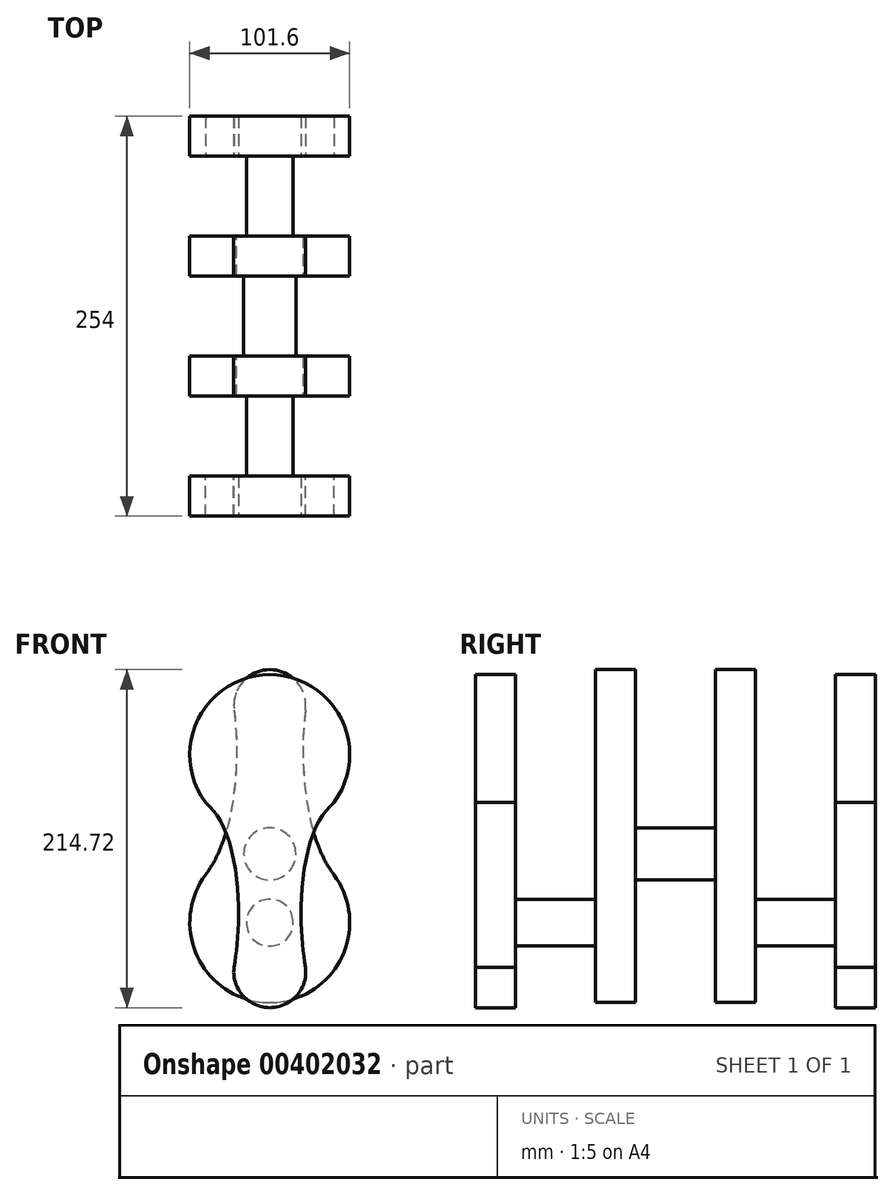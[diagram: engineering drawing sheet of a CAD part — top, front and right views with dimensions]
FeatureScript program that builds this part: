
annotation { "Feature Type Name" : "Feature", "Feature Type Description" : "" }
export const myFeature = defineFeature(function(context is Context, id is Id, definition is map)
    precondition{}
    {
        {
            var Q0;
            Q0=qCreatedBy(makeId("Front.planeOp"),FACE);
            var sketch = newSketch(context, id + "F0", { "sketchPlane" : qUnion([Q0])});
            skArc(sketch, "E0", {"start": v(-40.78, 30.29) * mm, "mid": v(0, -50.8) * mm, "end": v(40.78, 30.29) * mm});
            skArc(sketch, "E1", {"start": v(22.7, 135.07) * mm, "mid": v(0, 160.7) * mm, "end": v(-22.7, 135.07) * mm});
            skFitSpline(sketch, "E2", {"points": [v(-22.7, 135.07) * mm, v(-22.7, 83.37) * mm, v(-40.78, 30.29) * mm], "startDerivative": vector(13.12, -107.4) * mm, "endDerivative": vector(-66.36, -89.36) * mm});
            skLineSegment(sketch, "E3", {"start": v(0, 34.49) * mm, "end": v(0, 95.13) * mm, "construction": true});
            skFitSpline(sketch, "E4.MirrorCS", {"points": [v(22.7, 135.07) * mm, v(22.7, 83.37) * mm, v(40.78, 30.29) * mm], "startDerivative": vector(-13.12, -107.4) * mm, "endDerivative": vector(66.36, -89.36) * mm});
            skSolve(sketch);
        }
        {
            var Q0;
            Q0=makeQuery(id+"F0.imprint","IMPRINT",FACE,{"disambiguationData":[TD([[makeQuery(id+"F0.imprint","IMPRINT",EDGE,{"derivedFrom":sQuery(id+"F0.wireOp",EDGE,"E0")}),1.0]])]});
            extrude(context, id + "F1", {"entities" : qUnion([Q0]), "depth" : 25.4 * mm});
        }
        {
            var Q0;
            Q0=makeQuery(id+"F1.opExtrude","CAP_FACE",FACE,{"disambiguationData":[OSD([sQuery(id+"F0.wireOp",EDGE,"E0"),sQuery(id+"F0.wireOp",EDGE,"E1"),sQuery(id+"F0.wireOp",EDGE,"E2"),sQuery(id+"F0.wireOp",EDGE,"E4.MirrorCS")])],"isStart":false});
            var sketch = newSketch(context, id + "F2", { "sketchPlane" : qUnion([Q0])});
            skCircle(sketch, "E5", {"center": v(0, 0) * mm, "radius": 14.86 * mm});
            skSolve(sketch);
        }
        {
            var Q0;
            Q0 = qSketchRegion(id + "F2", true);
            extrude(context, id + "F3", {"entities" : qUnion([Q0]), "operationType" : NewBodyOperationType.ADD, "depth" : 50.8 * mm});
        }
        {
            var Q0;
            Q0=makeQuery(id+"F3.opExtrude","CAP_FACE",FACE,{"disambiguationData":[OSD([sQuery(id+"F2.wireOp",EDGE,"E5")])],"isStart":false});
            var sketch = newSketch(context, id + "F4", { "sketchPlane" : qUnion([Q0])});
            skArc(sketch, "E6.0.1", {"start": v(14.78, 155.28) * mm, "mid": v(0, 160.7) * mm, "end": v(-14.78, 155.28) * mm, "construction": true});
            skLineSegment(sketch, "E7", {"start": v(-56.31, 53.34) * mm, "end": v(133.14, 53.34) * mm, "construction": true});
            skArc(sketch, "E8.MirrorCS", {"start": v(-40.78, 76.4) * mm, "mid": v(0, 157.48) * mm, "end": v(40.78, 76.4) * mm});
            skFitSpline(sketch, "E9.MirrorCS", {"points": [v(-22.7, -28.4) * mm, v(-20.55, -10.85) * mm, v(-20.54, 22.91) * mm, v(-29.5, 61.2) * mm, v(-40.78, 76.4) * mm]});
            skFitSpline(sketch, "E10.MirrorCS", {"points": [v(40.78, 76.4) * mm, v(29.5, 61.2) * mm, v(20.54, 22.91) * mm, v(20.55, -10.85) * mm, v(22.7, -28.4) * mm]});
            skArc(sketch, "E11.MirrorCS", {"start": v(22.7, -28.4) * mm, "mid": v(0, -54.02) * mm, "end": v(-22.7, -28.4) * mm});
            skPoint(sketch, "E12.orphan", {"position": v(-22.7, 135.07) * mm});
            skPoint(sketch, "E13.orphan", {"position": v(22.7, 135.07) * mm});
            skPoint(sketch, "E6.0.0.start.orphan", {"position": v(40.78, 30.29) * mm});
            skPoint(sketch, "E6.0.2.end.orphan", {"position": v(-40.78, 30.29) * mm});
            skPoint(sketch, "E6.0.3.center.orphan", {"position": v(0, 0) * mm});
            skPoint(sketch, "E14.orphan", {"position": v(-22.7, -28.4) * mm});
            skLineSegment(sketch, "E15", {"start": v(0, 106.68) * mm, "end": v(0, 85.43) * mm, "construction": true});
            skFitSpline(sketch, "E16.MirrorCS", {"points": [v(-40.78, 76.4) * mm, v(-29.5, 61.2) * mm, v(-20.54, 22.91) * mm, v(-20.55, -10.85) * mm, v(-22.7, -28.4) * mm]});
            skSolve(sketch);
        }
        {
            var Q0;
            Q0 = qSketchRegion(id + "F4", true);
            extrude(context, id + "F5", {"entities" : qUnion([Q0]), "operationType" : NewBodyOperationType.ADD, "depth" : 25.4 * mm});
        }
        {
            var Q0;
            Q0=makeQuery(id+"F1.opExtrude","CAP_FACE",FACE,{"disambiguationData":[OSD([sQuery(id+"F0.wireOp",EDGE,"E0"),sQuery(id+"F0.wireOp",EDGE,"E1"),sQuery(id+"F0.wireOp",EDGE,"E2"),sQuery(id+"F0.wireOp",EDGE,"E4.MirrorCS")])],"isStart":true});
            var sketch = newSketch(context, id + "F6", { "sketchPlane" : qUnion([Q0])});
            skCircle(sketch, "E17", {"center": v(0, 43.69) * mm, "radius": 16.58 * mm});
            skSolve(sketch);
        }
        {
            var Q0;
            Q0 = qSketchRegion(id + "F6", true);
            extrude(context, id + "F7", {"entities" : qUnion([Q0]), "operationType" : NewBodyOperationType.ADD, "depth" : 25.4 * mm});
        }
        {
            var Q0;
            Q0=makeQuery(id+"F1.opExtrude","SWEPT_BODY",BODY,{"disambiguationData":[OSD([sQuery(id+"F0.wireOp",EDGE,"E0"),sQuery(id+"F0.wireOp",EDGE,"E1"),sQuery(id+"F0.wireOp",EDGE,"E2"),sQuery(id+"F0.wireOp",EDGE,"E4.MirrorCS")])]});
            var Q1;
            Q1=makeQuery(id+"F7.opExtrude","CAP_FACE",FACE,{"disambiguationData":[OSD([sQuery(id+"F6.wireOp",EDGE,"E17")])],"isStart":false});
            mirror(context, id + "F8", {"operationType" : NewBodyOperationType.ADD, "entities" : qUnion([Q0]), "mirrorPlane" : qUnion([Q1])});
        }
    });
